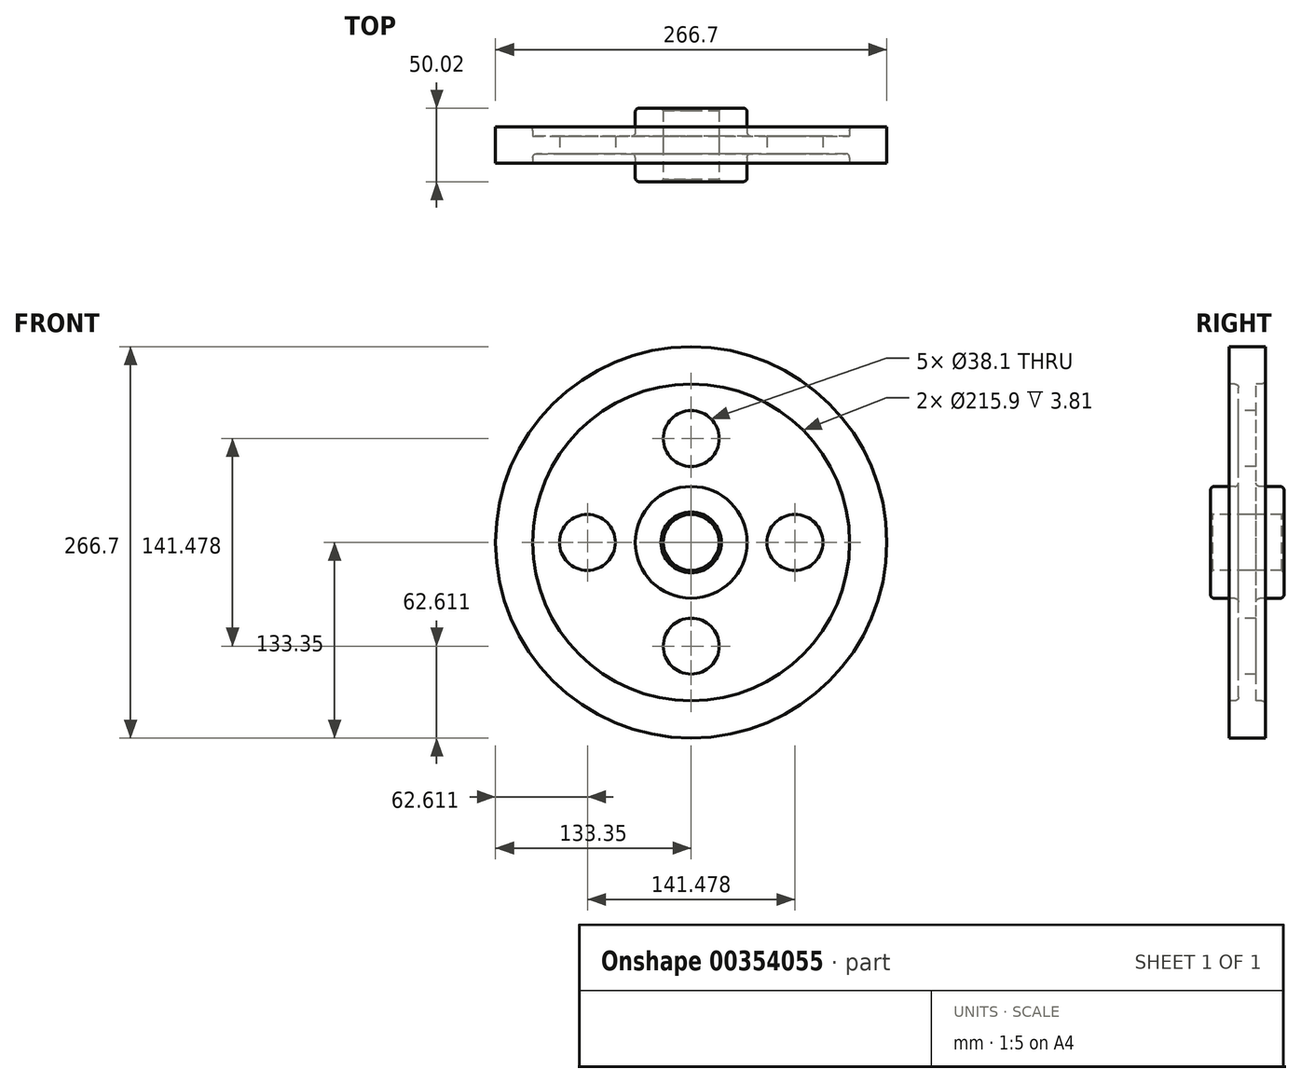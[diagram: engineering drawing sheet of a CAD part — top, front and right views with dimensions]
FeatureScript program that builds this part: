
annotation { "Feature Type Name" : "Feature", "Feature Type Description" : "" }
export const myFeature = defineFeature(function(context is Context, id is Id, definition is map)
    precondition{}
    {
        {
            var Q0;
            Q0=qCreatedBy(makeId("Right.planeOp"),FACE);
            var sketch = newSketch(context, id + "F0", { "sketchPlane" : qUnion([Q0])});
            skLineSegment(sketch, "E0", {"start": v(0, 0) * mm, "end": v(73.96, 0) * mm, "construction": true});
            skLineSegment(sketch, "E1.0", {"start": v(5.96, 19.05) * mm, "end": v(25.01, 19.05) * mm});
            skLineSegment(sketch, "E2.0", {"start": v(12.31, 38.1) * mm, "end": v(25.01, 38.1) * mm});
            skLineSegment(sketch, "E3.0", {"start": v(0, 133.35) * mm, "end": v(12.31, 133.35) * mm});
            skLineSegment(sketch, "E4.0", {"start": v(5.96, 107.95) * mm, "end": v(12.31, 107.95) * mm});
            skLineSegment(sketch, "E5.0", {"start": v(-49.88, 183.23) * mm, "end": v(73.96, 183.23) * mm});
            skLineSegment(sketch, "E6.0", {"start": v(5.96, 133.74) * mm, "end": v(12.31, 133.74) * mm});
            skLineSegment(sketch, "E7.0", {"start": v(5.96, 38.1) * mm, "end": v(5.96, 107.95) * mm});
            skLineSegment(sketch, "E8.0", {"start": v(-38.03, 171.38) * mm, "end": v(73.96, 171.38) * mm});
            skLineSegment(sketch, "E9.0", {"start": v(25.01, 19.05) * mm, "end": v(25.01, 38.1) * mm});
            skLineSegment(sketch, "E10.trimOffspring", {"start": v(25.01, 133.35) * mm, "end": v(25.01, 133.74) * mm});
            skLineSegment(sketch, "E11.trimOffspring", {"start": v(12.31, 133.35) * mm, "end": v(12.31, 133.74) * mm});
            skLineSegment(sketch, "E12", {"start": v(12.31, 133.74) * mm, "end": v(12.31, 133.35) * mm});
            skLineSegment(sketch, "E13.MirrorCS", {"start": v(5.96, 228.6) * mm, "end": v(5.96, 171.38) * mm});
            skLineSegment(sketch, "E14", {"start": v(12.31, 133.74) * mm, "end": v(12.31, 107.95) * mm});
            skLineSegment(sketch, "E15.trimOffspring", {"start": v(5.96, 133.74) * mm, "end": v(5.96, 132.96) * mm});
            skLineSegment(sketch, "E16", {"start": v(0, 0) * mm, "end": v(0, 133.35) * mm});
            skLineSegment(sketch, "E17", {"start": v(5.96, 19.05) * mm, "end": v(0, 19.05) * mm});
            skLineSegment(sketch, "E18", {"start": v(5.96, 38.1) * mm, "end": v(12.31, 38.1) * mm});
            skLineSegment(sketch, "E19.trimOffspring", {"start": v(5.96, 132.96) * mm, "end": v(5.96, 133.74) * mm});
            skLineSegment(sketch, "E20.MirrorCS", {"start": v(-5.96, 19.05) * mm, "end": v(0, 19.05) * mm});
            skLineSegment(sketch, "E21.MirrorCS", {"start": v(-5.96, 19.05) * mm, "end": v(-25.01, 19.05) * mm});
            skLineSegment(sketch, "E22.MirrorCS", {"start": v(-25.01, 19.05) * mm, "end": v(-25.01, 38.1) * mm});
            skLineSegment(sketch, "E23.MirrorCS", {"start": v(-5.96, 38.1) * mm, "end": v(-5.96, 107.95) * mm});
            skLineSegment(sketch, "E24.MirrorCS", {"start": v(-12.31, 38.1) * mm, "end": v(-25.01, 38.1) * mm});
            skLineSegment(sketch, "E25.MirrorCS", {"start": v(-5.96, 38.1) * mm, "end": v(-12.31, 38.1) * mm});
            skLineSegment(sketch, "E26.MirrorCS", {"start": v(-12.31, 133.74) * mm, "end": v(-12.31, 107.95) * mm});
            skLineSegment(sketch, "E27.MirrorCS", {"start": v(-5.96, 107.95) * mm, "end": v(-12.31, 107.95) * mm});
            skLineSegment(sketch, "E28.MirrorCS", {"start": v(-5.96, 133.74) * mm, "end": v(-12.31, 133.74) * mm});
            skLineSegment(sketch, "E29.MirrorCS", {"start": v(0, 133.35) * mm, "end": v(-12.31, 133.35) * mm});
            skSolve(sketch);
        }
        {
            var Q0;
            {var subQ0=sQuery(id+"F0.wireOp",EDGE,"E20.MirrorCS");Q0=makeQuery(id+"F0.imprint","IMPRINT",FACE,{"disambiguationData":[TD([[makeQuery(id+"F0.imprint","IMPRINT",EDGE,{"derivedFrom":subQ0}),1.0]])]});}
            var Q1;
            Q1=makeQuery(id+"F0.imprint","IMPRINT",FACE,{"disambiguationData":[TD([[makeQuery(id+"F0.imprint","IMPRINT",EDGE,{"derivedFrom":sQuery(id+"F0.wireOp",EDGE,"E1.0")}),1.0]])]});
            var Q2;
            Q2=sQuery(id+"F0.wireOp",EDGE,"E0");
            revolve(context, id + "F1", {"entities" : qUnion([Q0, Q1]), "axis" : qUnion([Q2]), "revolveType" : RevolveType.FULL});
        }
        {
            var Q0;
            Q0=makeQuery(id+"F1.opRevolve","SWEPT_FACE",FACE,{"disambiguationData":[OSD([sQuery(id+"F0.wireOp",EDGE,"E23.MirrorCS")])]});
            var sketch = newSketch(context, id + "F2", { "sketchPlane" : qUnion([Q0])});
            skLineSegment(sketch, "E30", {"start": v(0, 0) * mm, "end": v(0, 70.74) * mm});
            skCircle(sketch, "E31", {"center": v(0, 70.74) * mm, "radius": 19.05 * mm});
            skCircle(sketch, "E32.1.0", {"center": v(-70.74, 0) * mm, "radius": 19.05 * mm});
            skCircle(sketch, "E32.2.0", {"center": v(0, -70.74) * mm, "radius": 19.05 * mm});
            skPoint(sketch, "E32.center", {"position": v(0, 0) * mm});
            skCircle(sketch, "E33.1.3.0", {"center": v(70.74, 0) * mm, "radius": 19.05 * mm});
            skSolve(sketch);
        }
        {
            var Q0;
            Q0=makeQuery(id+"F2.imprint","IMPRINT",FACE,{"disambiguationData":[TD([[makeQuery(id+"F2.imprint","IMPRINT",EDGE,{"derivedFrom":sQuery(id+"F2.wireOp",EDGE,"E31")}),1.0]])]});
            var Q1;
            Q1=makeQuery(id+"F2.imprint","IMPRINT",FACE,{"disambiguationData":[TD([[makeQuery(id+"F2.imprint","IMPRINT",EDGE,{"derivedFrom":sQuery(id+"F2.wireOp",EDGE,"E33.1.3.0")}),1.0]])]});
            var Q2;
            Q2=makeQuery(id+"F2.imprint","IMPRINT",FACE,{"disambiguationData":[TD([[makeQuery(id+"F2.imprint","IMPRINT",EDGE,{"derivedFrom":sQuery(id+"F2.wireOp",EDGE,"E32.2.0")}),1.0]])]});
            var Q3;
            Q3=makeQuery(id+"F2.imprint","IMPRINT",FACE,{"disambiguationData":[TD([[makeQuery(id+"F2.imprint","IMPRINT",EDGE,{"derivedFrom":sQuery(id+"F2.wireOp",EDGE,"E32.1.0")}),1.0]])]});
            extrude(context, id + "F3", {"entities" : qUnion([Q0, Q1, Q2, Q3]), "operationType" : NewBodyOperationType.REMOVE, "oppositeDirection" : true, "depth" : 25.4 * mm});
        }
        {
            var Q0;
            Q0=makeQuery(id+"F1.opRevolve","SWEPT_EDGE",EDGE,{"disambiguationData":[OSD([sQuery(id+"F0.wireOp",EDGE,"E22.MirrorCS"),sQuery(id+"F0.wireOp",EDGE,"E24.MirrorCS")])]});
            var Q1;
            Q1=makeQuery(id+"F1.opRevolve","SWEPT_EDGE",EDGE,{"disambiguationData":[OSD([sQuery(id+"F0.wireOp",EDGE,"E23.MirrorCS"),sQuery(id+"F0.wireOp",EDGE,"E25.MirrorCS")])]});
            var Q2;
            Q2=makeQuery(id+"F1.opRevolve","SWEPT_EDGE",EDGE,{"disambiguationData":[OSD([sQuery(id+"F0.wireOp",EDGE,"E23.MirrorCS"),sQuery(id+"F0.wireOp",EDGE,"E27.MirrorCS")])]});
            var Q3;
            Q3=makeQuery(id+"F1.opRevolve","SWEPT_EDGE",EDGE,{"disambiguationData":[OSD([sQuery(id+"F0.wireOp",EDGE,"E2.0"),sQuery(id+"F0.wireOp",EDGE,"E9.0")])]});
            var Q4;
            Q4=makeQuery(id+"F1.opRevolve","SWEPT_EDGE",EDGE,{"disambiguationData":[OSD([sQuery(id+"F0.wireOp",EDGE,"E7.0"),sQuery(id+"F0.wireOp",EDGE,"E18")])]});
            var Q5;
            Q5=makeQuery(id+"F1.opRevolve","SWEPT_EDGE",EDGE,{"disambiguationData":[OSD([sQuery(id+"F0.wireOp",EDGE,"E4.0"),sQuery(id+"F0.wireOp",EDGE,"E14")])]});
            fillet(context, id + "F4", {"entities" : qUnion([Q0, Q1, Q2, Q3, Q4, Q5]), "radius" : 2.54 * mm, "tangentPropagation" : true, "allowEdgeOverflow" : false});
        }
        {
            var Q0;
            Q0=makeQuery(id+"F1.opRevolve","SWEPT_EDGE",EDGE,{"disambiguationData":[OSD([sQuery(id+"F0.wireOp",EDGE,"E21.MirrorCS"),sQuery(id+"F0.wireOp",EDGE,"E22.MirrorCS")])]});
            var Q1;
            Q1=makeQuery(id+"F1.opRevolve","SWEPT_EDGE",EDGE,{"disambiguationData":[OSD([sQuery(id+"F0.wireOp",EDGE,"E1.0"),sQuery(id+"F0.wireOp",EDGE,"E9.0")])]});
            chamfer(context, id + "F5", {"entities" : qUnion([Q0, Q1]), "width" : 1.59 * mm, "tangentPropagation" : true});
        }
    });
